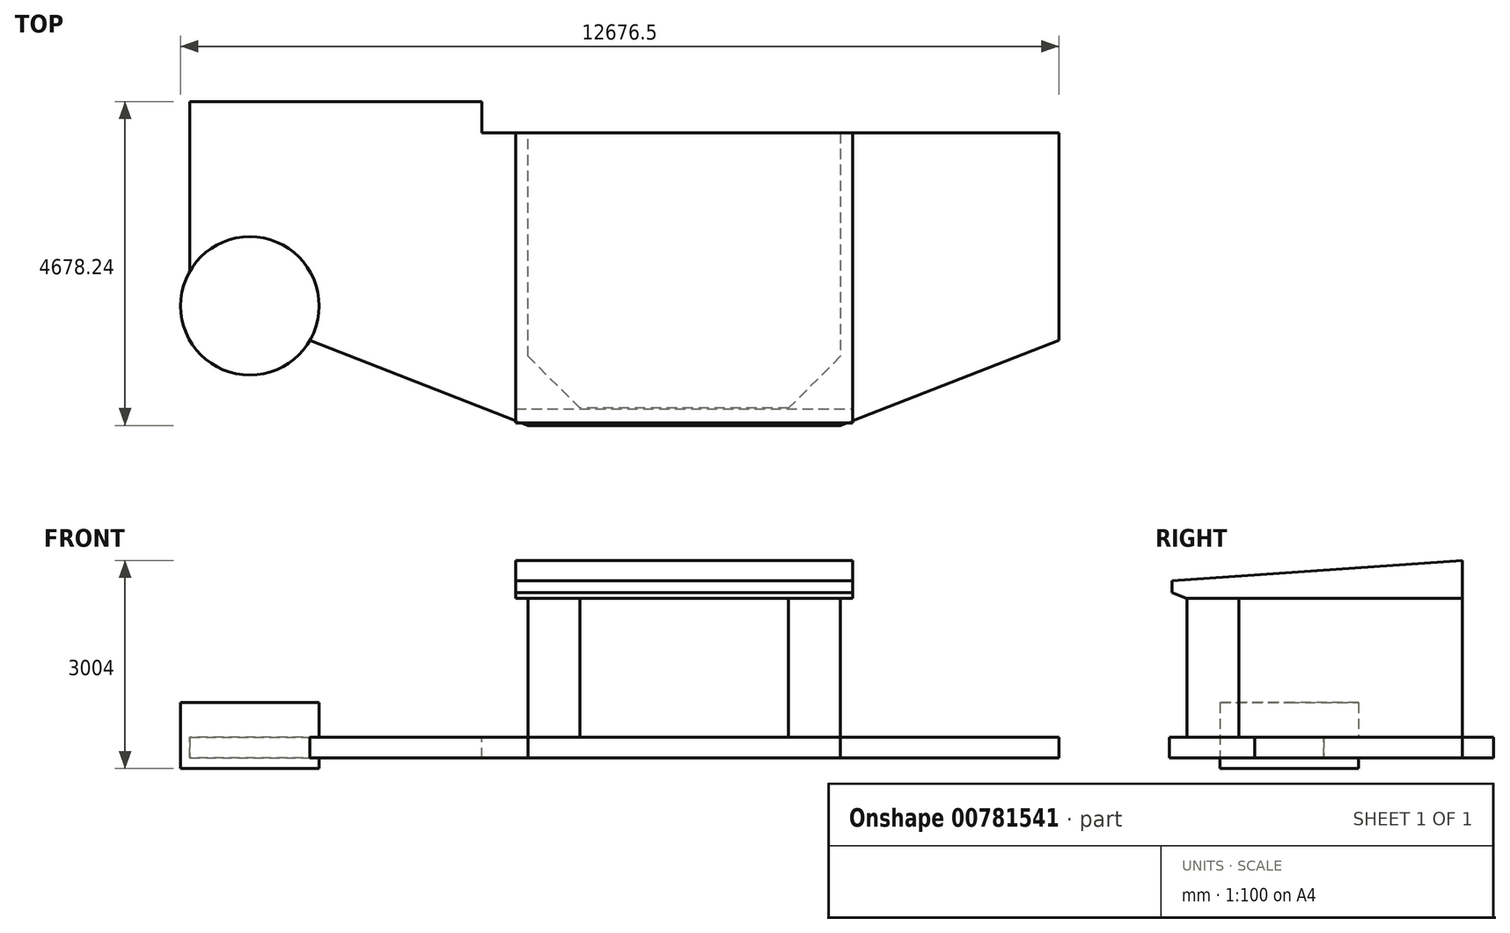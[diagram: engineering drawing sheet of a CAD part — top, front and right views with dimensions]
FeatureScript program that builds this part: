
annotation { "Feature Type Name" : "Feature", "Feature Type Description" : "" }
export const myFeature = defineFeature(function(context is Context, id is Id, definition is map)
    precondition{}
    {
        {
            var Q0;
            Q0=qCreatedBy(makeId("Top.planeOp"),FACE);
            var sketch = newSketch(context, id + "F0", { "sketchPlane" : qUnion([Q0])});
            skLineSegment(sketch, "E0", {"start": v(0, 0) * mm, "end": v(-28.46, 0) * mm});
            skLineSegment(sketch, "E1", {"start": v(0, 0) * mm, "end": v(-1530, 0) * mm});
            skLineSegment(sketch, "E2", {"start": v(-8330, 0) * mm, "end": v(-8330, 450) * mm});
            skLineSegment(sketch, "E3", {"start": v(-8330, 450) * mm, "end": v(-13950, 450) * mm});
            skLineSegment(sketch, "E4", {"start": v(-1530, 0) * mm, "end": v(-1530, 200) * mm});
            skLineSegment(sketch, "E5", {"start": v(-3100, 0) * mm, "end": v(-3100, 200) * mm});
            skLineSegment(sketch, "E6", {"start": v(-3450, 0) * mm, "end": v(-3450, 200) * mm});
            skLineSegment(sketch, "E7", {"start": v(-4240, 0) * mm, "end": v(-4240, 200) * mm});
            skLineSegment(sketch, "E8", {"start": v(-3100, 200) * mm, "end": v(-1530, 200) * mm});
            skLineSegment(sketch, "E9", {"start": v(-3450, 200) * mm, "end": v(-4240, 200) * mm});
            skLineSegment(sketch, "E10.trimOffspring", {"start": v(-3100, 0) * mm, "end": v(-3450, 0) * mm});
            skLineSegment(sketch, "E11.trimOffspring", {"start": v(-4240, 0) * mm, "end": v(-8330, 0) * mm});
            skLineSegment(sketch, "E12.bottom", {"start": v(-3100, 0) * mm, "end": v(-7572.1, 0) * mm});
            skLineSegment(sketch, "E13", {"start": v(-3150, 0) * mm, "end": v(-3150, -3228) * mm});
            skLineSegment(sketch, "E14", {"start": v(-3150, -3228) * mm, "end": v(-3900.24, -3978.24) * mm});
            skLineSegment(sketch, "E15", {"start": v(-5815, 0) * mm, "end": v(-5815, 200) * mm});
            skLineSegment(sketch, "E16", {"start": v(-6870, 0) * mm, "end": v(-6870, 200) * mm});
            skLineSegment(sketch, "E17", {"start": v(-10540, 450) * mm, "end": v(-10540, 650) * mm});
            skLineSegment(sketch, "E18", {"start": v(-12110, 450) * mm, "end": v(-12110, 650) * mm});
            skLineSegment(sketch, "E19", {"start": v(-12110, 650) * mm, "end": v(-10540, 650) * mm});
            skLineSegment(sketch, "E20", {"start": v(-6870, 200) * mm, "end": v(-5815, 200) * mm});
            skLineSegment(sketch, "E21", {"start": v(-4240, 0) * mm, "end": v(-3450, 0) * mm});
            skLineSegment(sketch, "E22", {"start": v(-3100, 0) * mm, "end": v(-1530, 0) * mm});
            skLineSegment(sketch, "E23", {"start": v(-3900.24, -3978.24) * mm, "end": v(-6910.24, -3978.24) * mm});
            skLineSegment(sketch, "E24", {"start": v(-6910.24, -3978.24) * mm, "end": v(-7660.48, -3228) * mm});
            skLineSegment(sketch, "E25", {"start": v(-7660.48, -3228) * mm, "end": v(-7660.48, 0) * mm});
            skSolve(sketch);
        }
        {
            var Q0;
            Q0=qCreatedBy(makeId("Top.planeOp"),FACE);
            var sketch = newSketch(context, id + "F1", { "sketchPlane" : qUnion([Q0])});
            skLineSegment(sketch, "E26", {"start": v(0, 0) * mm, "end": v(0, -3000) * mm});
            skLineSegment(sketch, "E27", {"start": v(0, -3000) * mm, "end": v(-3150, -4228.24) * mm});
            skLineSegment(sketch, "E28", {"start": v(-3150, -4228.24) * mm, "end": v(-7660.48, -4228.24) * mm});
            skLineSegment(sketch, "E29", {"start": v(-7660.48, -4228.24) * mm, "end": v(-10810.48, -3000) * mm});
            skLineSegment(sketch, "E30", {"start": v(-10810.48, -3000) * mm, "end": v(-12542.53, -2000) * mm});
            skLineSegment(sketch, "E31", {"start": v(-12542.53, -2000) * mm, "end": v(-12542.53, 450) * mm});
            skLineSegment(sketch, "E32", {"start": v(-12542.53, 450) * mm, "end": v(-8330, 450) * mm});
            skLineSegment(sketch, "E33", {"start": v(-8330, 450) * mm, "end": v(-8330, 0) * mm});
            skLineSegment(sketch, "E34", {"start": v(-8330, 0) * mm, "end": v(0, 0) * mm});
            skSolve(sketch);
        }
        {
            var Q0;
            Q0=qCreatedBy(makeId("Top.planeOp"),FACE);
            var sketch = newSketch(context, id + "F2", { "sketchPlane" : qUnion([Q0])});
            skCircle(sketch, "E35", {"center": v(-11676.5, -2500) * mm, "radius": 1000 * mm});
            skSolve(sketch);
        }
        {
            var Q0;
            Q0=makeQuery(id+"F2.imprint","IMPRINT",FACE,{"disambiguationData":[TD([[makeQuery(id+"F2.imprint","IMPRINT",EDGE,{"derivedFrom":sQuery(id+"F2.wireOp",EDGE,"E35")}),1.0]])]});
            extrude(context, id + "F3", {"entities" : qUnion([Q0]), "depth" : 500 * mm, "offsetDistance" : 25 * mm});
        }
        {
            var Q0;
            Q0=makeQuery(id+"F3.opExtrude","CAP_FACE",FACE,{"disambiguationData":[OSD([sQuery(id+"F2.wireOp",EDGE,"E35")])],"isStart":false});
            extrude(context, id + "F4", {"entities" : qUnion([Q0]), "operationType" : NewBodyOperationType.ADD, "oppositeDirection" : true, "depth" : 950 * mm, "offsetDistance" : 25 * mm});
        }
        {
            var Q0;
            Q0 = qSketchRegion(id + "F1", true);
            extrude(context, id + "F5", {"entities" : qUnion([Q0]), "operationType" : NewBodyOperationType.ADD, "oppositeDirection" : true, "depth" : 300 * mm, "offsetDistance" : 25 * mm});
        }
        {
            var Q0;
            {var subQ0=sQuery(id+"F0.wireOp",EDGE,"E13");Q0=makeQuery(id+"F0.imprint","IMPRINT",FACE,{"disambiguationData":[TD([[makeQuery(id+"F0.imprint","IMPRINT",EDGE,{"derivedFrom":subQ0}),-1.0]])]});}
            extrude(context, id + "F6", {"entities" : qUnion([Q0]), "operationType" : NewBodyOperationType.ADD, "depth" : 2010 * mm, "offsetDistance" : 25 * mm});
        }
        {
            var Q0;
            Q0=qCreatedBy(makeId("Right.planeOp"),FACE);
            cPlane(context, id + "F7", {"entities" : qUnion([Q0]), "cplaneType" : CPlaneType.OFFSET, "offset" : (3150 - 178) * mm, "oppositeDirection" : true, "width" : 150 * mm, "height" : 150 * mm});
        }
        {
            var Q0;
            Q0=qCreatedBy(id+"F7.planeOp",FACE);
            var sketch = newSketch(context, id + "F8", { "sketchPlane" : qUnion([Q0])});
            skLineSegment(sketch, "E36", {"start": v(0, 2010) * mm, "end": v(0, 2554) * mm});
            skLineSegment(sketch, "E37", {"start": v(0, 2554) * mm, "end": v(-4191.76, 2260.88) * mm});
            skLineSegment(sketch, "E38", {"start": v(0, 2010) * mm, "end": v(-3986.43, 2010) * mm});
            skLineSegment(sketch, "E39", {"start": v(-3986.43, 2010) * mm, "end": v(-4191.76, 2086.74) * mm});
            skLineSegment(sketch, "E40", {"start": v(-4191.76, 2260.88) * mm, "end": v(-4191.76, 2086.74) * mm});
            skPoint(sketch, "E41.orphan", {"position": v(-4192.73, 2087.1) * mm});
            skSolve(sketch);
        }
        {
            var Q0;
            Q0=makeQuery(id+"F8.imprint","IMPRINT",FACE,{"disambiguationData":[TD([[makeQuery(id+"F8.imprint","IMPRINT",EDGE,{"derivedFrom":sQuery(id+"F8.wireOp",EDGE,"E36")}),1.0]])]});
            extrude(context, id + "F9", {"entities" : qUnion([Q0]), "oppositeDirection" : true, "depth" : 4866.48 * mm, "offsetDistance" : 25 * mm});
        }
    });
